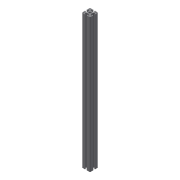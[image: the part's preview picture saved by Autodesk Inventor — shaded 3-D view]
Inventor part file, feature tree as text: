
AUTODESK INVENTOR PART (.ipt)
format: ipt  version: 2016 (Build 200138000, 138)  size: 219,648 bytes
history: native  units: mm
features: other x42, sketch x5, hole x4, extrude x1
ambient origin geometry x8: Origin, YZ Plane, XZ Plane, XY Plane, X Axis, Y Axis, Z Axis, Center Point
bodies: Solid1 (feature_tree)
feature tree (52):
  extrude  "Extrusion1"  [1 undecoded]
  hole  "Drilling 1"  [1 undecoded]
  hole  "Drilling 2"  [1 undecoded]
  hole  "Drilling 3"  [1 undecoded]
  hole  "Drilling 4"  [1 undecoded]
  other  "side_4d_XY"
  other  "side_4d_YZ"
  other  "side_4d_ZX"
  other  "side_4d_X"
  other  "side_4d_Y"
  other  "side_4d_Z"
  other  "side_4d_Center"
  other  "side_1a_XY"
  other  "side_1a_YZ"
  other  "side_1a_ZX"
  other  "side_1a_X"
  other  "side_1a_Y"
  other  "side_1a_Z"
  other  "side_1a_Center"
  other  "side_2b_XY"
  other  "side_2b_YZ"
  other  "side_2b_ZX"
  other  "side_2b_X"
  other  "side_2b_Y"
  other  "side_2b_Z"
  other  "side_2b_Center"
  other  "side_3c_XY"
  other  "side_3c_YZ"
  other  "side_3c_ZX"
  other  "side_3c_X"
  other  "side_3c_Y"
  other  "side_3c_Z"
  other  "side_3c_Center"
  other  "end_XY"
  other  "end_YZ"
  other  "end_ZX"
  other  "end_X"
  other  "end_Y"
  other  "end_Z"
  other  "end_Center"
  other  "start_XY"
  other  "start_YZ"
  other  "start_ZX"
  other  "start_X"
  other  "start_Y"
  other  "start_Z"
  other  "start_Center"
  sketch  "Skizze_1"  dims[d0=660.0mm d1=0.0mm]
  sketch  "Sketch2"  dims[d2=5.0mm d3=6.0mm d4=4.0mm d5=2.0mm d6=90.0deg d7=6000.0mm d8=0.0mm]
  sketch  "Sketch3"  dims[d9=5.0mm d10=6.0mm d11=4.0mm d12=2.0mm d13=90.0deg d14=6000.0mm d15=0.0mm]
  sketch  "Sketch4"  dims[d16=5.0mm d17=6.0mm d18=4.0mm d19=2.0mm d20=90.0deg d21=6000.0mm d22=0.0mm]
  sketch  "Sketch5"  dims[d23=5.0mm d24=6.0mm d25=4.0mm d26=2.0mm d27=90.0deg d28=6000.0mm d29=0.0mm]
note: 5 required parameter values undecoded (feature->parameter linkage not recoverable at this tier; creation-order binding heuristic only, values carry confidence <= 0.55)
